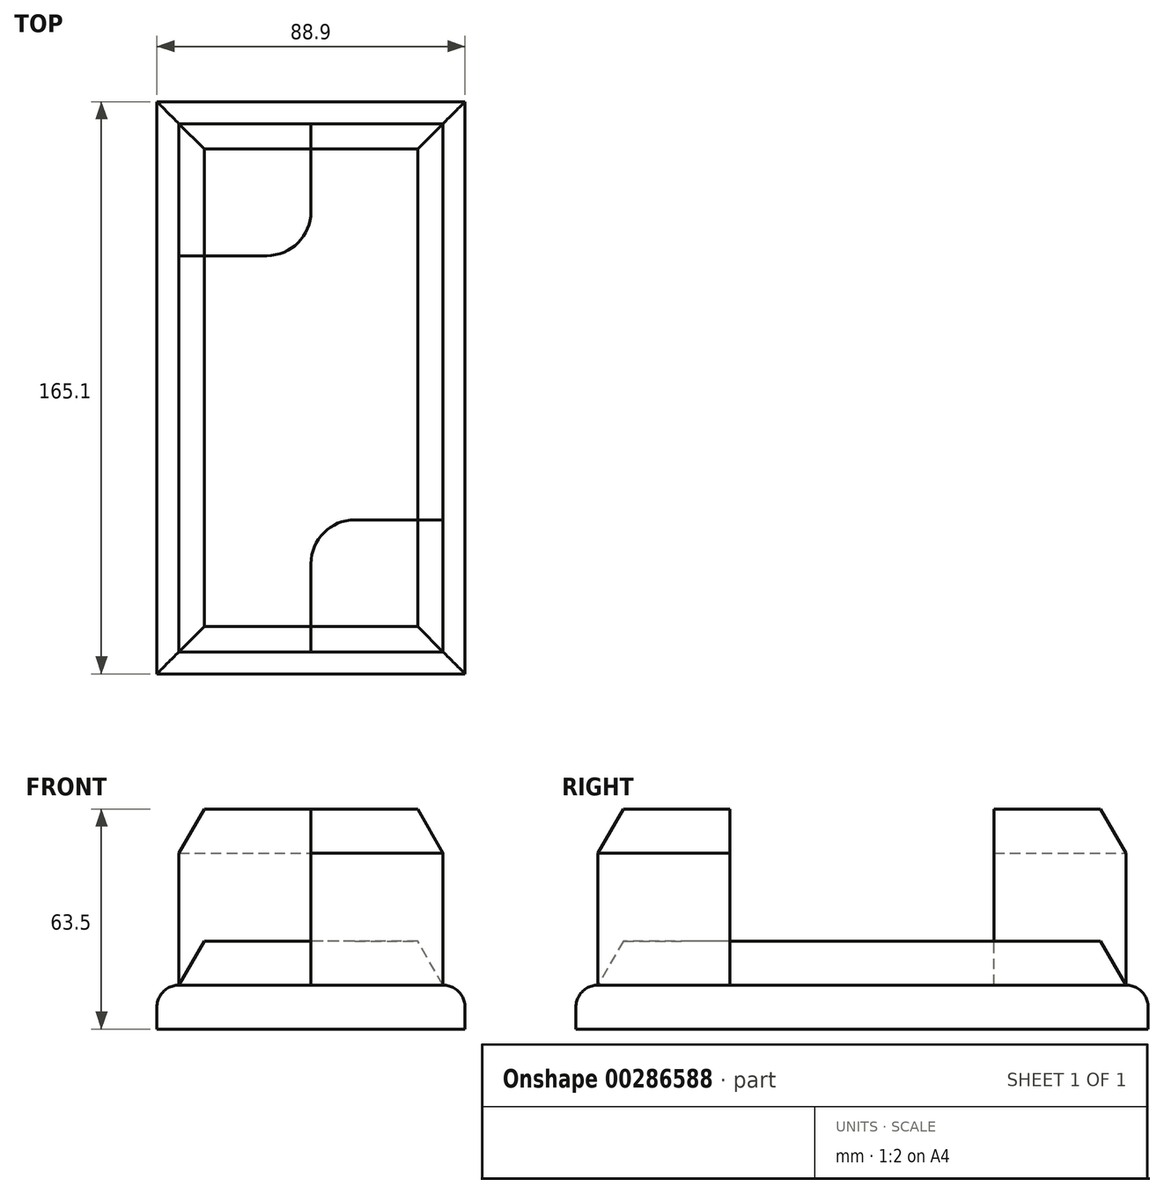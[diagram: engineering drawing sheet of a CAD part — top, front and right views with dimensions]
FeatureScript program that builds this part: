
annotation { "Feature Type Name" : "Feature", "Feature Type Description" : "" }
export const myFeature = defineFeature(function(context is Context, id is Id, definition is map)
    precondition{}
    {
        {
            var Q0;
            Q0=qCreatedBy(makeId("Top.planeOp"),FACE);
            var sketch = newSketch(context, id + "F0", { "sketchPlane" : qUnion([Q0])});
            skLineSegment(sketch, "E0", {"start": v(0, 76.2) * mm, "end": v(0, -76.2) * mm});
            skLineSegment(sketch, "E1", {"start": v(0, -76.2) * mm, "end": v(76.2, -76.2) * mm});
            skLineSegment(sketch, "E2", {"start": v(76.2, -76.2) * mm, "end": v(76.2, 76.2) * mm});
            skLineSegment(sketch, "E3", {"start": v(76.2, 76.2) * mm, "end": v(0, 76.2) * mm});
            skPoint(sketch, "E4", {"position": v(38.1, 76.2) * mm});
            skPoint(sketch, "E5", {"position": v(38.1, -76.2) * mm});
            skLineSegment(sketch, "E6", {"start": v(25.4, 38.1) * mm, "end": v(0, 38.1) * mm});
            skLineSegment(sketch, "E7", {"start": v(38.1, -76.2) * mm, "end": v(38.1, -50.8) * mm});
            skLineSegment(sketch, "E8", {"start": v(50.8, -38.1) * mm, "end": v(76.2, -38.1) * mm});
            skLineSegment(sketch, "E9", {"start": v(38.1, 76.2) * mm, "end": v(38.1, 50.8) * mm});
            skPoint(sketch, "E10.visualSharp", {"position": v(38.1, 38.1) * mm});
            skArc(sketch, "E10.filletArc", {"start": v(25.4, 38.1) * mm, "mid": v(34.38, 41.82) * mm, "end": v(38.1, 50.8) * mm});
            skPoint(sketch, "E11.visualSharp", {"position": v(38.1, -38.1) * mm});
            skArc(sketch, "E11.filletArc", {"start": v(50.8, -38.1) * mm, "mid": v(41.82, -41.82) * mm, "end": v(38.1, -50.8) * mm});
            skLineSegment(sketch, "E12.0", {"start": v(82.55, -82.55) * mm, "end": v(82.55, 82.55) * mm});
            skLineSegment(sketch, "E13.0", {"start": v(-6.35, -82.55) * mm, "end": v(82.55, -82.55) * mm});
            skLineSegment(sketch, "E14.0", {"start": v(-6.35, 82.55) * mm, "end": v(-6.35, -82.55) * mm});
            skLineSegment(sketch, "E15.0", {"start": v(82.55, 82.55) * mm, "end": v(-6.35, 82.55) * mm});
            skSolve(sketch);
        }
        {
            var Q0;
            Q0 = qSketchRegion(id + "F0", true);
            extrude(context, id + "F1", {"entities" : qUnion([Q0]), "depth" : 12.7 * mm});
        }
        {
            var Q0;
            {var subQ9=sQuery(id+"F0.wireOp",EDGE,"E6");Q0=makeQuery(id+"F0.imprint","IMPRINT",FACE,{"disambiguationData":[TD([[makeQuery(id+"F0.imprint","IMPRINT",EDGE,{"derivedFrom":subQ9}),1.0]])]});}
            extrude(context, id + "F2", {"entities" : qUnion([Q0]), "operationType" : NewBodyOperationType.ADD, "depth" : 25.4 * mm});
        }
        {
            var Q0;
            {var subQ4=sQuery(id+"F0.wireOp",EDGE,"E6");Q0=makeQuery(id+"F0.imprint","IMPRINT",FACE,{"disambiguationData":[TD([[makeQuery(id+"F0.imprint","IMPRINT",EDGE,{"derivedFrom":subQ4}),-1.0]])]});}
            var Q1;
            {var subQ1=sQuery(id+"F0.wireOp",EDGE,"E7");Q1=makeQuery(id+"F0.imprint","IMPRINT",FACE,{"disambiguationData":[TD([[makeQuery(id+"F0.imprint","IMPRINT",EDGE,{"derivedFrom":subQ1}),-1.0]])]});}
            extrude(context, id + "F3", {"entities" : qUnion([Q0, Q1]), "operationType" : NewBodyOperationType.ADD, "depth" : 63.5 * mm});
        }
        {
            var Q0;
            Q0=makeQuery(id+"F1.opExtrude","CAP_EDGE",EDGE,{"disambiguationData":[OSD([sQuery(id+"F0.wireOp",EDGE,"E14.0")])],"isStart":false});
            var Q1;
            Q1=makeQuery(id+"F1.opExtrude","CAP_EDGE",EDGE,{"disambiguationData":[OSD([sQuery(id+"F0.wireOp",EDGE,"E13.0")])],"isStart":false});
            var Q2;
            Q2=makeQuery(id+"F1.opExtrude","CAP_EDGE",EDGE,{"disambiguationData":[OSD([sQuery(id+"F0.wireOp",EDGE,"E12.0")])],"isStart":false});
            var Q3;
            Q3=makeQuery(id+"F1.opExtrude","CAP_EDGE",EDGE,{"disambiguationData":[OSD([sQuery(id+"F0.wireOp",EDGE,"E15.0")])],"isStart":false});
            fillet(context, id + "F4", {"entities" : qUnion([Q0, Q1, Q2, Q3]), "radius" : 6.35 * mm, "tangentPropagation" : true, "allowEdgeOverflow" : false});
        }
        {
            var Q0;
            Q0=makeQuery(id+"F2.opExtrude","CAP_EDGE",EDGE,{"disambiguationData":[OSD([sQuery(id+"F0.wireOp",EDGE,"E3")])],"isStart":false});
            var Q1;
            Q1=makeQuery(id+"F2.opExtrude","CAP_EDGE",EDGE,{"disambiguationData":[OSD([sQuery(id+"F0.wireOp",EDGE,"E2")])],"isStart":false});
            var Q2;
            Q2=makeQuery(id+"F2.opExtrude","CAP_EDGE",EDGE,{"disambiguationData":[OSD([sQuery(id+"F0.wireOp",EDGE,"E0")])],"isStart":false});
            var Q3;
            Q3=makeQuery(id+"F2.opExtrude","CAP_EDGE",EDGE,{"disambiguationData":[OSD([sQuery(id+"F0.wireOp",EDGE,"E1")])],"isStart":false});
            var Q4;
            Q4=makeQuery(id+"F3.opExtrude","CAP_EDGE",EDGE,{"disambiguationData":[OSD([sQuery(id+"F0.wireOp",EDGE,"E1")])],"isStart":false});
            var Q5;
            Q5=makeQuery(id+"F3.opExtrude","CAP_EDGE",EDGE,{"disambiguationData":[OSD([sQuery(id+"F0.wireOp",EDGE,"E2")])],"isStart":false});
            var Q6;
            Q6=makeQuery(id+"F3.opExtrude","CAP_EDGE",EDGE,{"disambiguationData":[OSD([sQuery(id+"F0.wireOp",EDGE,"E3")])],"isStart":false});
            var Q7;
            Q7=makeQuery(id+"F3.opExtrude","CAP_EDGE",EDGE,{"disambiguationData":[OSD([sQuery(id+"F0.wireOp",EDGE,"E0")])],"isStart":false});
            chamfer(context, id + "F5", {"entities" : qUnion([Q0, Q1, Q2, Q3, Q4, Q5, Q6, Q7]), "chamferType" : ChamferType.OFFSET_ANGLE, "width" : 12.7 * mm, "oppositeDirection" : true, "angle" : 30 * degree, "tangentPropagation" : true});
        }
    });
